annotation { "Feature Type Name" : "Feature", "Feature Type Description" : "" }
export const myFeature = defineFeature(function(context is Context, id is Id, definition is map)
    precondition{}
    {
        {
            var Q0;
            Q0=qCreatedBy(makeId("Top.planeOp"),FACE);
            var sketch = newSketch(context, id + "F0", { "sketchPlane" : qUnion([Q0])});
            skLineSegment(sketch, "E0.bottom", {"start": v(-894.88, 501.73) * mm, "end": v(1605.12, 501.73) * mm});
            skLineSegment(sketch, "E0.top", {"start": v(-894.88, -498.27) * mm, "end": v(1605.12, -498.27) * mm});
            skLineSegment(sketch, "E0.left", {"start": v(-894.88, 501.73) * mm, "end": v(-894.88, -498.27) * mm});
            skLineSegment(sketch, "E0.right", {"start": v(1605.12, 501.73) * mm, "end": v(1605.12, -498.27) * mm});
            skLineSegment(sketch, "E1.bottom", {"start": v(-844.88, -348.27) * mm, "end": v(-744.88, -348.27) * mm});
            skLineSegment(sketch, "E1.top", {"start": v(-844.88, -448.27) * mm, "end": v(-744.88, -448.27) * mm});
            skLineSegment(sketch, "E1.left", {"start": v(-844.88, -348.27) * mm, "end": v(-844.88, -448.27) * mm});
            skLineSegment(sketch, "E1.right", {"start": v(-744.88, -348.27) * mm, "end": v(-744.88, -448.27) * mm});
            skLineSegment(sketch, "E2.bottom", {"start": v(-844.88, 451.73) * mm, "end": v(-744.88, 451.73) * mm});
            skLineSegment(sketch, "E2.top", {"start": v(-844.88, 351.73) * mm, "end": v(-744.88, 351.73) * mm});
            skLineSegment(sketch, "E2.left", {"start": v(-844.88, 451.73) * mm, "end": v(-844.88, 351.73) * mm});
            skLineSegment(sketch, "E2.right", {"start": v(-744.88, 451.73) * mm, "end": v(-744.88, 351.73) * mm});
            skLineSegment(sketch, "E3.bottom", {"start": v(-844.88, 451.73) * mm, "end": v(1555.12, 451.73) * mm, "construction": true});
            skLineSegment(sketch, "E3.top", {"start": v(-844.88, -448.27) * mm, "end": v(1555.12, -448.27) * mm, "construction": true});
            skLineSegment(sketch, "E3.left", {"start": v(-844.88, 451.73) * mm, "end": v(-844.88, -448.27) * mm, "construction": true});
            skLineSegment(sketch, "E3.right", {"start": v(1555.12, 451.73) * mm, "end": v(1555.12, -448.27) * mm, "construction": true});
            skLineSegment(sketch, "E4.bottom", {"start": v(1455.12, -348.27) * mm, "end": v(1555.12, -348.27) * mm});
            skLineSegment(sketch, "E4.top", {"start": v(1455.12, -448.27) * mm, "end": v(1555.12, -448.27) * mm});
            skLineSegment(sketch, "E4.left", {"start": v(1455.12, -348.27) * mm, "end": v(1455.12, -448.27) * mm});
            skLineSegment(sketch, "E4.right", {"start": v(1555.12, -348.27) * mm, "end": v(1555.12, -448.27) * mm});
            skLineSegment(sketch, "E5.bottom", {"start": v(1455.12, 451.73) * mm, "end": v(1555.12, 451.73) * mm});
            skLineSegment(sketch, "E5.top", {"start": v(1455.12, 351.73) * mm, "end": v(1555.12, 351.73) * mm});
            skLineSegment(sketch, "E5.left", {"start": v(1455.12, 451.73) * mm, "end": v(1455.12, 351.73) * mm});
            skLineSegment(sketch, "E5.right", {"start": v(1555.12, 451.73) * mm, "end": v(1555.12, 351.73) * mm});
            skSolve(sketch);
        }
        {
            var Q0;
            Q0=makeQuery(id+"F0.imprint","IMPRINT",FACE,{"disambiguationData":[TD([[makeQuery(id+"F0.imprint","IMPRINT",EDGE,{"derivedFrom":sQuery(id+"F0.wireOp",EDGE,"E2.bottom")}),-1.0]])]});
            var Q1;
            Q1=makeQuery(id+"F0.imprint","IMPRINT",FACE,{"disambiguationData":[TD([[makeQuery(id+"F0.imprint","IMPRINT",EDGE,{"derivedFrom":sQuery(id+"F0.wireOp",EDGE,"E5.bottom")}),-1.0]])]});
            var Q2;
            Q2=makeQuery(id+"F0.imprint","IMPRINT",FACE,{"disambiguationData":[TD([[makeQuery(id+"F0.imprint","IMPRINT",EDGE,{"derivedFrom":sQuery(id+"F0.wireOp",EDGE,"E4.bottom")}),-1.0]])]});
            var Q3;
            Q3=makeQuery(id+"F0.imprint","IMPRINT",FACE,{"disambiguationData":[TD([[makeQuery(id+"F0.imprint","IMPRINT",EDGE,{"derivedFrom":sQuery(id+"F0.wireOp",EDGE,"E1.bottom")}),-1.0]])]});
            extrude(context, id + "F1", {"entities" : qUnion([Q0, Q1, Q2, Q3]), "depth" : 700 * mm});
        }
        {
            var Q0;
            Q0=makeQuery(id+"F1.opExtrude","CAP_FACE",FACE,{"disambiguationData":[OSD([sQuery(id+"F0.wireOp",EDGE,"E2.bottom"),sQuery(id+"F0.wireOp",EDGE,"E2.top"),sQuery(id+"F0.wireOp",EDGE,"E2.left"),sQuery(id+"F0.wireOp",EDGE,"E2.right")])],"isStart":false});
            var sketch = newSketch(context, id + "F2", { "sketchPlane" : qUnion([Q0])});
            skLineSegment(sketch, "E6.0", {"start": v(-894.88, 501.73) * mm, "end": v(1605.12, 501.73) * mm});
            skLineSegment(sketch, "E6.1", {"start": v(-894.88, 501.73) * mm, "end": v(-894.88, -498.27) * mm});
            skLineSegment(sketch, "E6.2", {"start": v(-894.88, -498.27) * mm, "end": v(1605.12, -498.27) * mm});
            skLineSegment(sketch, "E6.3", {"start": v(1605.12, 501.73) * mm, "end": v(1605.12, -498.27) * mm});
            skSolve(sketch);
        }
        {
            var Q0;
            Q0=makeQuery(id+"F2.imprint","IMPRINT",FACE,{"disambiguationData":[TD([[makeQuery(id+"F2.imprint","IMPRINT",EDGE,{"derivedFrom":sQuery(id+"F2.wireOp",EDGE,"E6.0")}),-1.0]])]});
            var Q1;
            Q1=makeQuery(id+"F2.imprint","IMPRINT",FACE,{"disambiguationData":[TD([[makeQuery(id+"F2.imprint","IMPRINT",EDGE,{"derivedFrom":makeQuery(id+"F1.opExtrude","CAP_EDGE",EDGE,{"disambiguationData":[OSD([sQuery(id+"F0.wireOp",EDGE,"E2.bottom")])],"isStart":false})}),-1.0]])]});
            extrude(context, id + "F3", {"entities" : qUnion([Q0, Q1]), "depth" : 25 * mm});
        }
        {
            var Q0;
            Q0=makeQuery(id+"F1.opExtrude","SWEPT_FACE",FACE,{"disambiguationData":[OSD([sQuery(id+"F0.wireOp",EDGE,"E1.top")])]});
            var sketch = newSketch(context, id + "F4", { "sketchPlane" : qUnion([Q0])});
            skLineSegment(sketch, "E7", {"start": v(-794.88, 714.74) * mm, "end": v(-794.88, -41.16) * mm, "construction": true});
            skLineSegment(sketch, "E8", {"start": v(-993.24, 600) * mm, "end": v(-645.2, 600) * mm, "construction": true});
            skLineSegment(sketch, "E9", {"start": v(-992.21, 400) * mm, "end": v(-606.18, 400) * mm, "construction": true});
            skLineSegment(sketch, "E10", {"start": v(-1017.88, 200) * mm, "end": v(-587.7, 200) * mm, "construction": true});
            skCircle(sketch, "E11", {"center": v(-794.88, 600) * mm, "radius": 25 * mm});
            skCircle(sketch, "E12", {"center": v(-794.88, 400) * mm, "radius": 25 * mm});
            skCircle(sketch, "E13", {"center": v(-794.88, 200) * mm, "radius": 25 * mm});
            skSolve(sketch);
        }
        {
            var Q0;
            Q0=makeQuery(id+"F4.imprint","IMPRINT",FACE,{"disambiguationData":[TD([[makeQuery(id+"F4.imprint","IMPRINT",EDGE,{"derivedFrom":sQuery(id+"F4.wireOp",EDGE,"E11")}),1.0]])]});
            var Q1;
            Q1=makeQuery(id+"F4.imprint","IMPRINT",FACE,{"disambiguationData":[TD([[makeQuery(id+"F4.imprint","IMPRINT",EDGE,{"derivedFrom":sQuery(id+"F4.wireOp",EDGE,"E12")}),1.0]])]});
            var Q2;
            Q2=makeQuery(id+"F4.imprint","IMPRINT",FACE,{"disambiguationData":[TD([[makeQuery(id+"F4.imprint","IMPRINT",EDGE,{"derivedFrom":sQuery(id+"F4.wireOp",EDGE,"E13")}),1.0]])]});
            extrude(context, id + "F5", {"entities" : qUnion([Q0, Q1, Q2]), "operationType" : NewBodyOperationType.REMOVE, "endBound" : BoundingType.THROUGH_ALL, "oppositeDirection" : true, "depth" : 100 * mm});
        }
        {
            var Q0;
            Q0=makeQuery(id+"F1.opExtrude","SWEPT_FACE",FACE,{"disambiguationData":[OSD([sQuery(id+"F0.wireOp",EDGE,"E4.top")])]});
            var sketch = newSketch(context, id + "F6", { "sketchPlane" : qUnion([Q0])});
            skLineSegment(sketch, "E14", {"start": v(1505.12, 777.3) * mm, "end": v(1505.12, -53.44) * mm, "construction": true});
            skLineSegment(sketch, "E15", {"start": v(902.09, 600) * mm, "end": v(1197.68, 600) * mm, "construction": true});
            skLineSegment(sketch, "E16", {"start": v(894.4, 400) * mm, "end": v(1224.16, 400) * mm, "construction": true});
            skLineSegment(sketch, "E17", {"start": v(907.21, 200) * mm, "end": v(1302.76, 200) * mm, "construction": true});
            skCircle(sketch, "E18", {"center": v(1505.12, 600) * mm, "radius": 25 * mm});
            skCircle(sketch, "E19", {"center": v(1505.12, 400) * mm, "radius": 25 * mm});
            skCircle(sketch, "E20", {"center": v(1505.12, 200) * mm, "radius": 25 * mm});
            skSolve(sketch);
        }
        {
            var Q0;
            Q0 = qSketchRegion(id + "F6", true);
            extrude(context, id + "F7", {"entities" : qUnion([Q0]), "operationType" : NewBodyOperationType.REMOVE, "endBound" : BoundingType.THROUGH_ALL, "oppositeDirection" : true, "depth" : 25 * mm});
        }
        {
            var Q0;
            Q0=makeQuery(id+"F3.opExtrude","CAP_FACE",FACE,{"disambiguationData":[OSD([sQuery(id+"F2.wireOp",EDGE,"E6.0"),sQuery(id+"F2.wireOp",EDGE,"E6.1"),sQuery(id+"F2.wireOp",EDGE,"E6.2"),sQuery(id+"F2.wireOp",EDGE,"E6.3")])],"isStart":false});
            var sketch = newSketch(context, id + "F8", { "sketchPlane" : qUnion([Q0])});
            skText(sketch, "E21", { "text": "Les Unelles", "fontName": "OpenSans-Regular.ttf"});
            const initialGuessF8  = {"E21": [-0.60733, -0.25454, 1, 0, 0.1902]};
            skSetInitialGuess(sketch, initialGuessF8);
            skSolve(sketch);
        }
        {
            var Q0;
            Q0 = qSketchRegion(id + "F8", true);
            extrude(context, id + "F9", {"entities" : qUnion([Q0]), "operationType" : NewBodyOperationType.REMOVE, "oppositeDirection" : true, "depth" : 5 * mm});
        }
        {
            var Q0;
            {var subQ0=sQuery(id+"F2.wireOp",EDGE,"E6.3");var subQ1=sQuery(id+"F2.wireOp",EDGE,"E6.0");var subQ2=sQuery(id+"F2.wireOp",EDGE,"E6.2");var subQ3=sQuery(id+"F2.wireOp",EDGE,"E6.1");Q0=makeQuery(id+"F9.boolean.opBoolean","SPLIT",FACE,{"disambiguationData":[TD([makeQuery(id+"F3.opExtrude","SWEPT_FACE",FACE,{"disambiguationData":[OSD([subQ1])]})])],"derivedFrom":makeQuery(id+"F3.opExtrude","CAP_FACE",FACE,{"disambiguationData":[OSD([subQ1,subQ3,subQ2,subQ0])],"isStart":false})});}
            fillet(context, id + "F10", {"entities" : qUnion([Q0]), "radius" : 25 * mm, "allowEdgeOverflow" : false});
        }
    });